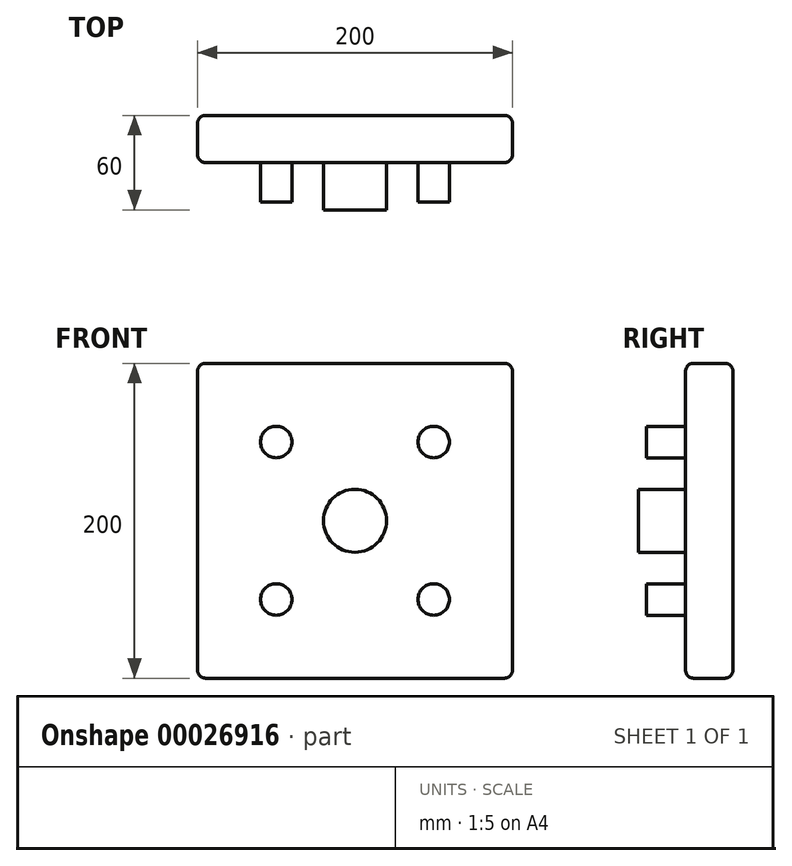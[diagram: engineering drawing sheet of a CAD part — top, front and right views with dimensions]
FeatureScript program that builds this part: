
annotation { "Feature Type Name" : "Feature", "Feature Type Description" : "" }
export const myFeature = defineFeature(function(context is Context, id is Id, definition is map)
    precondition{}
    {
        {
            var Q0;
            Q0=qCreatedBy(makeId("Front.planeOp"),FACE);
            var sketch = newSketch(context, id + "F0", { "sketchPlane" : qUnion([Q0])});
            skLineSegment(sketch, "E0.bottom", {"start": v(-100, 100) * mm, "end": v(100, 100) * mm});
            skLineSegment(sketch, "E0.top", {"start": v(-100, -100) * mm, "end": v(100, -100) * mm});
            skLineSegment(sketch, "E0.left", {"start": v(-100, 100) * mm, "end": v(-100, -100) * mm});
            skLineSegment(sketch, "E0.right", {"start": v(100, 100) * mm, "end": v(100, -100) * mm});
            skSolve(sketch);
        }
        {
            var Q0;
            Q0=qSketchRegion(id+"F0",true);
            extrude(context, id + "F1", {"entities" : qUnion([Q0]), "depth" : 30 * mm});
        }
        {
            var Q0;
            Q0=makeQuery(id+"F1.opExtrude","CAP_FACE",FACE,{"disambiguationData":[OSD([sQuery(id+"F0.wireOp",EDGE,"E0.bottom"),sQuery(id+"F0.wireOp",EDGE,"E0.top"),sQuery(id+"F0.wireOp",EDGE,"E0.left"),sQuery(id+"F0.wireOp",EDGE,"E0.right")])],"isStart":false});
            var sketch = newSketch(context, id + "F2", { "sketchPlane" : qUnion([Q0])});
            skCircle(sketch, "E1", {"center": v(0, 0) * mm, "radius": 20 * mm});
            skSolve(sketch);
        }
        {
            var Q0;
            Q0=makeQuery(id+"F2.imprint","IMPRINT",FACE,{"disambiguationData":[TD([[makeQuery(id+"F2.imprint","IMPRINT",EDGE,{"derivedFrom":sQuery(id+"F2.wireOp",EDGE,"E1")}),1.0]])]});
            extrude(context, id + "F3", {"entities" : qUnion([Q0]), "operationType" : NewBodyOperationType.ADD, "depth" : 30 * mm});
        }
        {
            var Q0;
            Q0=makeQuery(id+"F1.opExtrude","CAP_FACE",FACE,{"disambiguationData":[OSD([sQuery(id+"F0.wireOp",EDGE,"E0.bottom"),sQuery(id+"F0.wireOp",EDGE,"E0.top"),sQuery(id+"F0.wireOp",EDGE,"E0.left"),sQuery(id+"F0.wireOp",EDGE,"E0.right")])],"isStart":false});
            var sketch = newSketch(context, id + "F4", { "sketchPlane" : qUnion([Q0])});
            skCircle(sketch, "E2", {"center": v(-50, -50) * mm, "radius": 10 * mm});
            skCircle(sketch, "E3.0.1.0", {"center": v(-50, 50) * mm, "radius": 10 * mm});
            skCircle(sketch, "E3.1.0.0", {"center": v(50, -50) * mm, "radius": 10 * mm});
            skCircle(sketch, "E3.1.1.0", {"center": v(50, 50) * mm, "radius": 10 * mm});
            skLineSegment(sketch, "E3.direction1", {"start": v(-50, -50) * mm, "end": v(50, -50) * mm, "construction": true});
            skLineSegment(sketch, "E3.direction2", {"start": v(-50, -50) * mm, "end": v(-50, 50) * mm, "construction": true});
            skLineSegment(sketch, "E4", {"start": v(-66.92, 0) * mm, "end": v(60.8, 0) * mm});
            skLineSegment(sketch, "E5", {"start": v(0, -49.75) * mm, "end": v(0, 68.34) * mm});
            skSolve(sketch);
        }
        {
            var Q0;
            Q0=makeQuery(id+"F1.opExtrude","SWEPT_FACE",FACE,{"disambiguationData":[OSD([sQuery(id+"F0.wireOp",EDGE,"E0.right")])]});
            var Q1;
            Q1=makeQuery(id+"F1.opExtrude","SWEPT_FACE",FACE,{"disambiguationData":[OSD([sQuery(id+"F0.wireOp",EDGE,"E0.top")])]});
            var Q2;
            Q2=makeQuery(id+"F1.opExtrude","CAP_EDGE",EDGE,{"disambiguationData":[OSD([sQuery(id+"F0.wireOp",EDGE,"E0.top")])],"isStart":true});
            var Q3;
            Q3=makeQuery(id+"F1.opExtrude","SWEPT_FACE",FACE,{"disambiguationData":[OSD([sQuery(id+"F0.wireOp",EDGE,"E0.left")])]});
            var Q4;
            Q4=makeQuery(id+"F1.opExtrude","SWEPT_FACE",FACE,{"disambiguationData":[OSD([sQuery(id+"F0.wireOp",EDGE,"E0.bottom")])]});
            fillet(context, id + "F5", {"entities" : qUnion([Q0, Q1, Q2, Q3, Q4]), "radius" : 5 * mm, "tangentPropagation" : true, "allowEdgeOverflow" : false});
        }
        {
            var Q0;
            Q0 = qSketchRegion(id + "F4", true);
            extrude(context, id + "F6", {"entities" : qUnion([Q0]), "operationType" : NewBodyOperationType.ADD, "depth" : 25 * mm});
        }
    });
